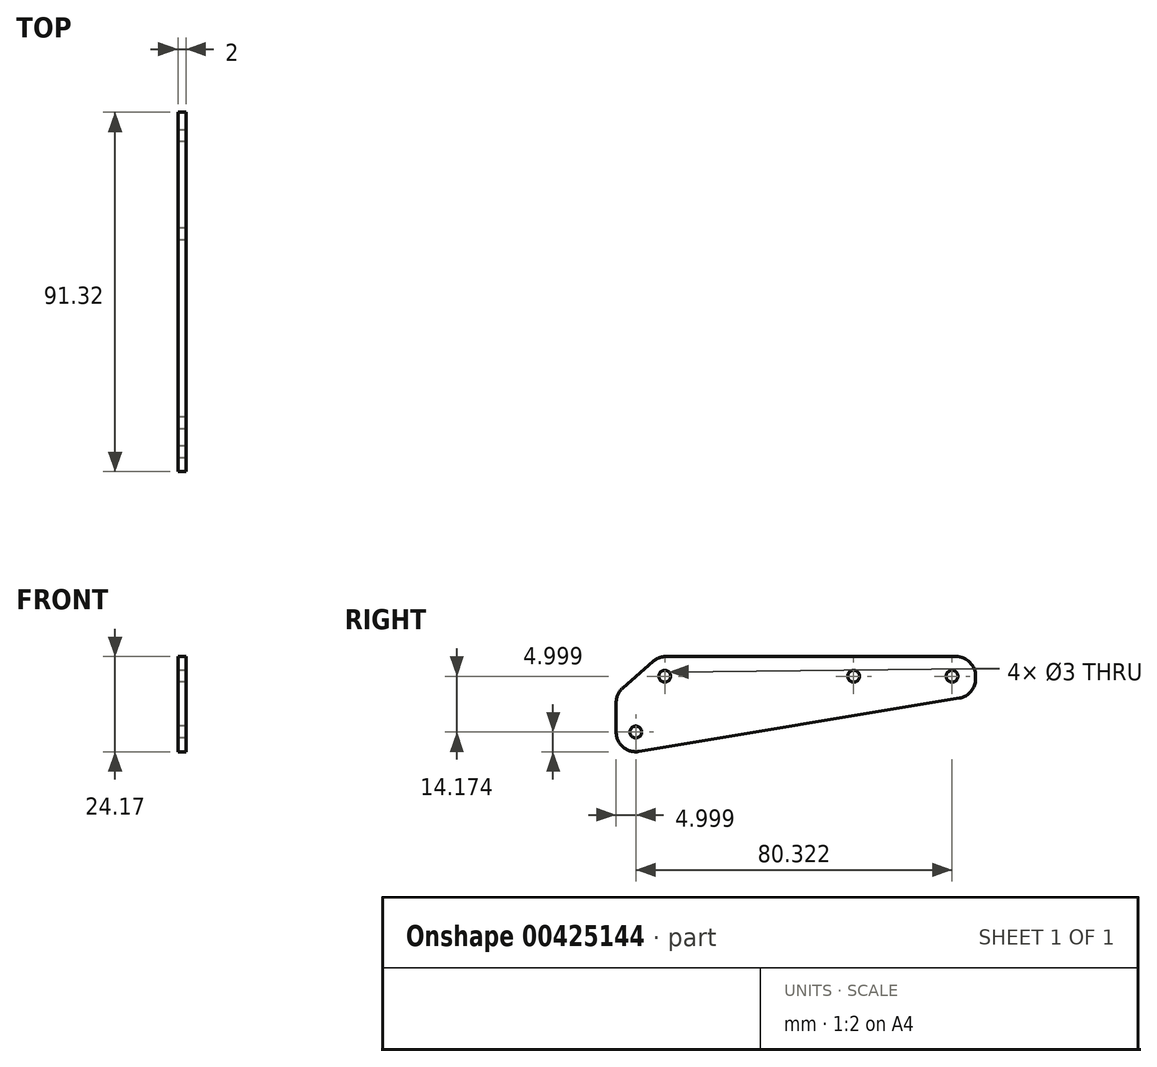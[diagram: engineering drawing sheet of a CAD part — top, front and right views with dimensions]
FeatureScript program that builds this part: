
annotation { "Feature Type Name" : "Feature", "Feature Type Description" : "" }
export const myFeature = defineFeature(function(context is Context, id is Id, definition is map)
    precondition{}
    {
        {
            var Q0;
            Q0=qCreatedBy(makeId("Right.planeOp"),FACE);
            var sketch = newSketch(context, id + "F0", { "sketchPlane" : qUnion([Q0])});
            skLineSegment(sketch, "E0", {"start": v(-31.25, 32.46) * mm, "end": v(42.45, 32.46) * mm});
            skLineSegment(sketch, "E1", {"start": v(47.45, 27.46) * mm, "end": v(47.45, 26.84) * mm});
            skLineSegment(sketch, "E2", {"start": v(43.27, 21.91) * mm, "end": v(-38.05, 8.36) * mm});
            skLineSegment(sketch, "E3", {"start": v(-43.87, 13.29) * mm, "end": v(-43.87, 20.79) * mm});
            skLineSegment(sketch, "E4", {"start": v(-42.16, 24.55) * mm, "end": v(-34.54, 31.22) * mm});
            skPoint(sketch, "E5.visualSharp", {"position": v(47.45, 32.46) * mm});
            skArc(sketch, "E5.filletArc", {"start": v(47.45, 27.46) * mm, "mid": v(45.99, 31) * mm, "end": v(42.45, 32.46) * mm});
            skPoint(sketch, "E6.visualSharp", {"position": v(47.45, 22.6) * mm});
            skArc(sketch, "E6.filletArc", {"start": v(43.27, 21.91) * mm, "mid": v(46.27, 23.61) * mm, "end": v(47.45, 26.84) * mm});
            skPoint(sketch, "E7.visualSharp", {"position": v(-43.87, 7.39) * mm});
            skArc(sketch, "E7.filletArc", {"start": v(-43.87, 13.29) * mm, "mid": v(-42.1, 9.47) * mm, "end": v(-38.05, 8.36) * mm});
            skPoint(sketch, "E8.visualSharp", {"position": v(-33.13, 32.46) * mm});
            skArc(sketch, "E8.filletArc", {"start": v(-31.25, 32.46) * mm, "mid": v(-33, 32.14) * mm, "end": v(-34.54, 31.22) * mm});
            skPoint(sketch, "E9.visualSharp", {"position": v(-43.87, 23.05) * mm});
            skArc(sketch, "E9.filletArc", {"start": v(-42.16, 24.55) * mm, "mid": v(-43.42, 22.85) * mm, "end": v(-43.87, 20.79) * mm});
            skSolve(sketch);
        }
        {
            var Q0;
            Q0 = qSketchRegion(id + "F0", true);
            extrude(context, id + "F1", {"entities" : qUnion([Q0]), "depth" : 2 * mm});
        }
        {
            var Q0;
            Q0=qCreatedBy(makeId("Right.planeOp"),FACE);
            var sketch = newSketch(context, id + "F2", { "sketchPlane" : qUnion([Q0])});
            skPoint(sketch, "E10", {"position": v(41.45, 27.46) * mm});
            skPoint(sketch, "E11", {"position": v(16.45, 27.46) * mm});
            skSolve(sketch);
        }
        {
            var Q0;
            Q0=sQuery(id+"F2.wireOp",VERTEX,"E10");
            var Q1;
            Q1=sQuery(id+"F2.wireOp",VERTEX,"E11");
            var Q2;
            Q2=makeQuery(id+"F1.opExtrude","SWEPT_BODY",BODY,{"disambiguationData":[OSD([sQuery(id+"F0.wireOp",EDGE,"E0"),sQuery(id+"F0.wireOp",EDGE,"E1"),sQuery(id+"F0.wireOp",EDGE,"E2"),sQuery(id+"F0.wireOp",EDGE,"E3"),sQuery(id+"F0.wireOp",EDGE,"E4"),sQuery(id+"F0.wireOp",EDGE,"E5.filletArc"),sQuery(id+"F0.wireOp",EDGE,"E6.filletArc"),sQuery(id+"F0.wireOp",EDGE,"E7.filletArc"),sQuery(id+"F0.wireOp",EDGE,"E8.filletArc"),sQuery(id+"F0.wireOp",EDGE,"E9.filletArc")])]});
            hole(context, id + "F3", {"style" : HoleStyle.SIMPLE, "endStyle" : HoleEndStyle.THROUGH, "oppositeDirection" : true, "holeDiameter" : 3 * mm, "isTappedThrough" : true, "tappedDepth" : 12 * mm, "tapClearance" : 3, "locations" : qUnion([Q0, Q1]), "scope" : qUnion([Q2])});
        }
        {
            var Q0;
            Q0=qCreatedBy(makeId("Right.planeOp"),FACE);
            var sketch = newSketch(context, id + "F4", { "sketchPlane" : qUnion([Q0])});
            skPoint(sketch, "E12", {"position": v(-38.87, 13.29) * mm});
            skPoint(sketch, "E13", {"position": v(-31.52, 27.46) * mm});
            skSolve(sketch);
        }
        {
            var Q0;
            Q0=sQuery(id+"F4.wireOp",VERTEX,"E13");
            var Q1;
            Q1=sQuery(id+"F4.wireOp",VERTEX,"E12");
            var Q2;
            Q2=makeQuery(id+"F1.opExtrude","SWEPT_BODY",BODY,{"disambiguationData":[OSD([sQuery(id+"F0.wireOp",EDGE,"E0"),sQuery(id+"F0.wireOp",EDGE,"E1"),sQuery(id+"F0.wireOp",EDGE,"E2"),sQuery(id+"F0.wireOp",EDGE,"E3"),sQuery(id+"F0.wireOp",EDGE,"E4"),sQuery(id+"F0.wireOp",EDGE,"E5.filletArc"),sQuery(id+"F0.wireOp",EDGE,"E6.filletArc"),sQuery(id+"F0.wireOp",EDGE,"E7.filletArc"),sQuery(id+"F0.wireOp",EDGE,"E8.filletArc"),sQuery(id+"F0.wireOp",EDGE,"E9.filletArc")])]});
            hole(context, id + "F5", {"style" : HoleStyle.SIMPLE, "endStyle" : HoleEndStyle.THROUGH, "oppositeDirection" : true, "holeDiameter" : 3 * mm, "isTappedThrough" : true, "tappedDepth" : 12 * mm, "tapClearance" : 3, "locations" : qUnion([Q0, Q1]), "scope" : qUnion([Q2])});
        }
    });
